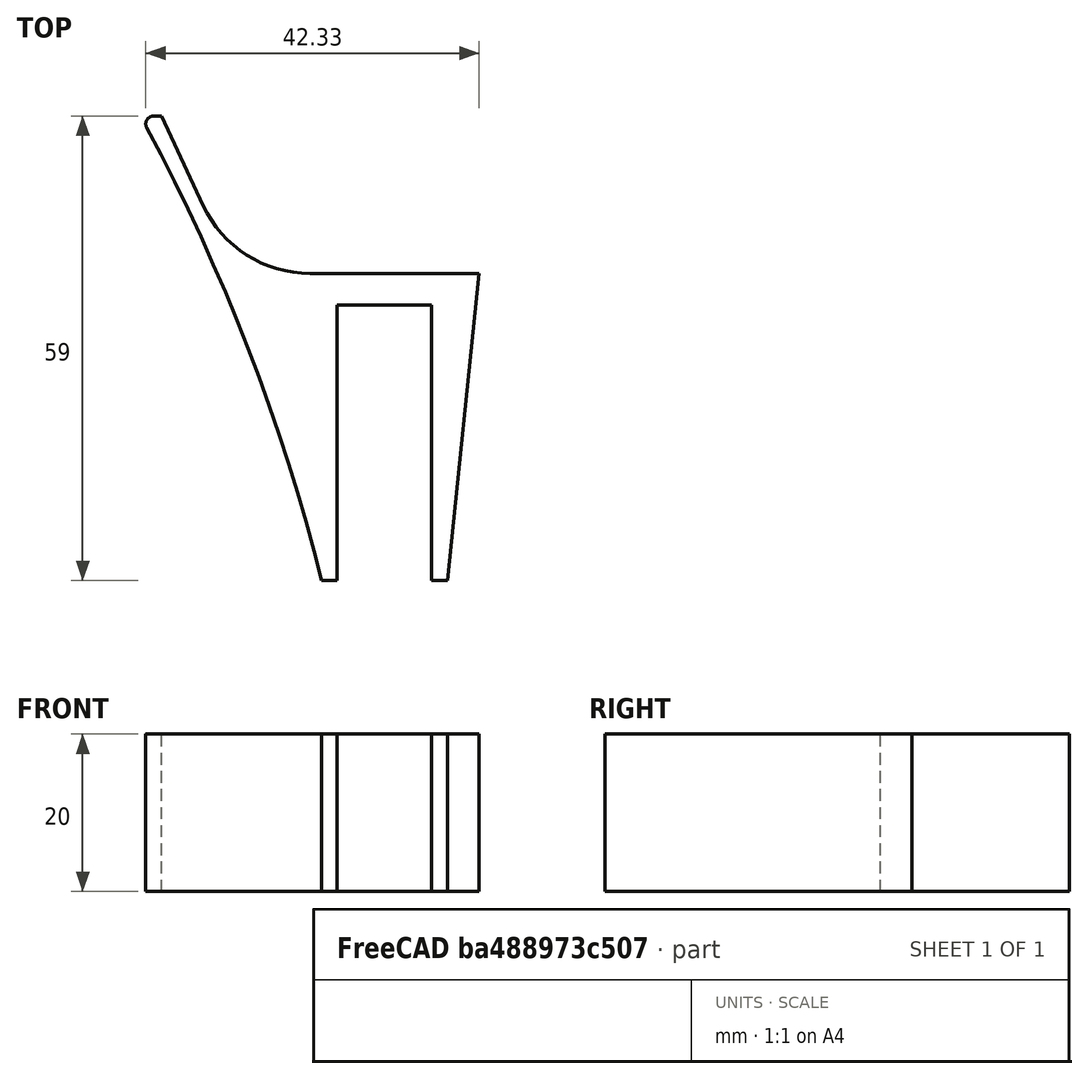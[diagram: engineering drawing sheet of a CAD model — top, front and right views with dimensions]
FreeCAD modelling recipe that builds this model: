
FCSTD DOCUMENT  (FreeCAD 2022.111R30764 (Git))
Label: cat bed bracket
License: All rights reserved
LicenseURL: http://en.wikipedia.org/wiki/All_rights_reserved
objects: Sketcher::SketchObject×1, PartDesign::Pad×1, PartDesign::Body×1
note: 5 computed .brp shape members not serialized (recipe doc carries the construction recipe); baked Part::Feature solids carry a one-line shape summary decoded from their .brp

FEATURE [Sketcher::SketchObject] Sketch
  FullyConstrained = true
  TreeRank = 11
  sketch-geometry (13):
    g0: LineSegment StartX=0 StartY=0 StartZ=0 EndX=0 EndY=-35 EndZ=0
    g1: LineSegment StartX=0 StartY=-35 StartZ=0 EndX=2 EndY=-35 EndZ=0
    g2: LineSegment StartX=2 StartY=-35 StartZ=0 EndX=6 EndY=4 EndZ=0
    g3: LineSegment StartX=6 StartY=4 StartZ=0 EndX=-15.4439 EndY=4 EndZ=0
    g4: LineSegment StartX=-29.0386 StartY=12.6607 StartZ=0 EndX=-34.3262 EndY=24 EndZ=0
    g5: LineSegment StartX=-34.3262 StartY=24 StartZ=0 EndX=-35.3262 EndY=24 EndZ=0
    g6: LineSegment StartX=-14 StartY=-35 StartZ=0 EndX=-12 EndY=-35 EndZ=0
    g7: LineSegment StartX=-12 StartY=-35 StartZ=0 EndX=-12 EndY=0 EndZ=0
    g8: LineSegment StartX=-12 StartY=0 StartZ=0 EndX=0 EndY=0 EndZ=0
    g9: ArcOfCircle CenterX=-256.549 CenterY=-95.5815 CenterZ=0 NormalX=0 NormalY=0 NormalZ=1 AngleXU=0 Radius=250 StartAngle=0.244763 EndAngle=0.492053
    g10: ArcOfCircle CenterX=-15.4439 CenterY=19 CenterZ=0 NormalX=0 NormalY=0 NormalZ=1 AngleXU=0 Radius=15 StartAngle=3.57792 EndAngle=4.71239
    g11: GeomPoint [constr] X=-25 Y=4 Z=0
    g12: ArcOfCircle CenterX=-35.3262 CenterY=23 CenterZ=0 NormalX=0 NormalY=0 NormalZ=1 AngleXU=0 Radius=1 StartAngle=1.5708 EndAngle=3.63365
  constraints (36):
    c: Coincident(g-1,g0)
    c: PointOnObject(g0,g-2)
    c: Coincident(g0,g1)
    c: Horizontal(g1)
    c: Coincident(g1,g2)
    c: Coincident(g2,g3)
    c: Horizontal(g3)
    c: Coincident(g4,g5)
    c: Horizontal(g5)
    c: Horizontal(g6)
    c: Coincident(g6,g7)
    c: PointOnObject(g7,g-1)
    c: Coincident(g7,g8)
    c: Coincident(g8,g0)
    c: Horizontal(g6,g0)
    c: DistanceY(g0,g0) = 35
    c: DistanceX(g1,g1) = 2
    c: DistanceX(g6,g6) = 2
    c: DistanceX(g6,g0) = 12
    c: DistanceY(g0,g2) = 4
    c: Vertical(g7)
    c: DistanceX(g0,g2) = 6
    c: DistanceX(g11,g7) = 13
    c: Coincident(g9,g6)
    c: PointOnObject(g11,g3)
    c: PointOnObject(g11,g4)
    c: Tangent(g3,g10) = 1.5708
    c: Tangent(g4,g10) = 1.5708
    c: Diameter(g10) = 30
    c: Tangent(g5,g12) = -1.5708
    c: Tangent(g9,g12) = 1.5708
    c: Diameter(g12) = 2
    c: DistanceX(g5,g5) = 1
    c: Angle(g3,g4) = 2.00713
    c: Diameter(g9) = 500
    c: DistanceY(g3,g4) = 20
FEATURE [PartDesign::Pad] Pad
  AddSubType = 0
  AlongSketchNormal = false
  CheckUpToFaceLimits = true
  ClaimChildren = false
  Direction = (0,0,1)
  Fit = 0
  FitJoin = 0
  InnerFit = 0
  InnerFitJoin = 0
  InnerTaperAngle = 0
  InnerTaperAngleRev = 0
  Length = 20
  Length2 = 100
  Linearize = true
  NewSolid = false
  Profile = -> Sketch
  Suppress = false
  TreeRank = 12
  Type = 0
  _ProfileBasedVersion = 1
FEATURE [PartDesign::Body] Body
  AutoGroupSolids = false
  ExportMode = 0
  Group = -> [Sketch,Pad]
  Origin = -> Origin
  Tip = -> Pad
  TreeRank = 10
  _ExportChildren = -> [Pad]
  _GroupVersion = 1
